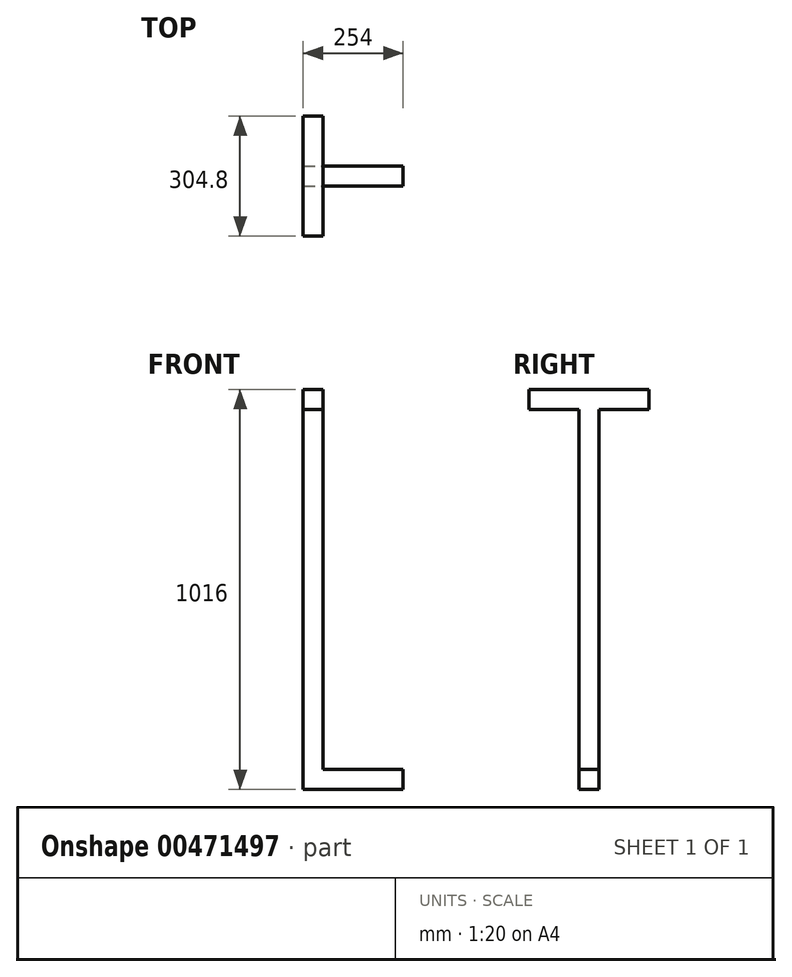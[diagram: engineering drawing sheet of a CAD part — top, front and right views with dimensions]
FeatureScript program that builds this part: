
annotation { "Feature Type Name" : "Feature", "Feature Type Description" : "" }
export const myFeature = defineFeature(function(context is Context, id is Id, definition is map)
    precondition{}
    {
        {
            var Q0;
            Q0=qCreatedBy(makeId("Front.planeOp"),FACE);
            var sketch = newSketch(context, id + "F0", { "sketchPlane" : qUnion([Q0])});
            skLineSegment(sketch, "E0", {"start": v(0, 0) * mm, "end": v(-203.2, 0) * mm});
            skLineSegment(sketch, "E1", {"start": v(-203.2, 0) * mm, "end": v(-203.2, 965.2) * mm});
            skLineSegment(sketch, "E2", {"start": v(-254, 965.2) * mm, "end": v(-254, -50.8) * mm});
            skLineSegment(sketch, "E3", {"start": v(-254, -50.8) * mm, "end": v(0, -50.8) * mm});
            skLineSegment(sketch, "E4", {"start": v(0, -50.8) * mm, "end": v(0, 0) * mm});
            skLineSegment(sketch, "E5", {"start": v(-203.2, 965.2) * mm, "end": v(-254, 965.2) * mm});
            skSolve(sketch);
        }
        {
            var Q0;
            Q0=makeQuery(id+"F0.imprint","IMPRINT",FACE,{"disambiguationData":[TD([[makeQuery(id+"F0.imprint","IMPRINT",EDGE,{"derivedFrom":sQuery(id+"F0.wireOp",EDGE,"E0")}),1.0]])]});
            extrude(context, id + "F1", {"entities" : qUnion([Q0]), "endBound" : BoundingType.SYMMETRIC, "depth" : 50.8 * mm, "offsetDistance" : 25.4 * mm});
        }
        {
            var Q0;
            Q0=makeQuery(id+"F1.opExtrude","CAP_FACE",FACE,{"disambiguationData":[OSD([sQuery(id+"F0.wireOp",EDGE,"E0"),sQuery(id+"F0.wireOp",EDGE,"E1"),sQuery(id+"F0.wireOp",EDGE,"E2"),sQuery(id+"F0.wireOp",EDGE,"E3"),sQuery(id+"F0.wireOp",EDGE,"E4"),sQuery(id+"F0.wireOp",EDGE,"E5")])],"isStart":false});
            var sketch = newSketch(context, id + "F2", { "sketchPlane" : qUnion([Q0])});
            skLineSegment(sketch, "E6.bottom", {"start": v(-254, 965.2) * mm, "end": v(-203.2, 965.2) * mm});
            skLineSegment(sketch, "E6.top", {"start": v(-254, 914.4) * mm, "end": v(-203.2, 914.4) * mm});
            skLineSegment(sketch, "E6.left", {"start": v(-254, 965.2) * mm, "end": v(-254, 914.4) * mm});
            skLineSegment(sketch, "E6.right", {"start": v(-203.2, 965.2) * mm, "end": v(-203.2, 914.4) * mm});
            skSolve(sketch);
        }
        {
            var Q0;
            Q0=makeQuery(id+"F2.imprint","IMPRINT",FACE,{"disambiguationData":[TD([[makeQuery(id+"F2.imprint","IMPRINT",EDGE,{"derivedFrom":sQuery(id+"F2.wireOp",EDGE,"E6.bottom")}),1.0]])]});
            extrude(context, id + "F3", {"entities" : qUnion([Q0]), "operationType" : NewBodyOperationType.ADD, "depth" : 127 * mm, "offsetDistance" : 25.4 * mm});
        }
        {
            var Q0;
            Q0=makeQuery(id+"F1.opExtrude","SWEPT_BODY",BODY,{"disambiguationData":[OSD([sQuery(id+"F0.wireOp",EDGE,"E0"),sQuery(id+"F0.wireOp",EDGE,"E1"),sQuery(id+"F0.wireOp",EDGE,"E2"),sQuery(id+"F0.wireOp",EDGE,"E3"),sQuery(id+"F0.wireOp",EDGE,"E4"),sQuery(id+"F0.wireOp",EDGE,"E5")])]});
            var Q1;
            Q1=qCreatedBy(makeId("Front.planeOp"),FACE);
            mirror(context, id + "F4", {"operationType" : NewBodyOperationType.ADD, "entities" : qUnion([Q0]), "mirrorPlane" : qUnion([Q1])});
        }
        {
            var Q0;
            {var subQ0=makeQuery(id+"F3.boolean.opBoolean","MERGE",FACE,{"derivedFrom":[makeQuery(id+"F1.opExtrude","SWEPT_FACE",FACE,{"disambiguationData":[OSD([sQuery(id+"F0.wireOp",EDGE,"E2")])]}),makeQuery(id+"F3.opExtrude","SWEPT_FACE",FACE,{"disambiguationData":[OSD([sQuery(id+"F2.wireOp",EDGE,"E6.left")])]})]});Q0=makeQuery(id+"F4.boolean.opBoolean","MERGE",FACE,{"derivedFrom":[subQ0,makeQuery(id+"F4.opPattern","COPY",FACE,{"derivedFrom":subQ0,"instanceName":"1"})]});}
            var sketch = newSketch(context, id + "F5", { "sketchPlane" : qUnion([Q0])});
            skCircle(sketch, "E7", {"center": v(-127, 939.8) * mm, "radius": 9.53 * mm});
            skSolve(sketch);
        }
        {
            var Q0;
            Q0=sQuery(id+"F5.wireOp",EDGE,"E7");
            extrude(context, id + "F6", {"bodyType" : ToolBodyType.SURFACE, "surfaceEntities" : qUnion([Q0]), "depth" : 406.4 * mm, "offsetDistance" : 25.4 * mm});
        }
        {
            var Q0;
            Q0=makeQuery(id+"F6.opExtrude","SWEPT_BODY",BODY,{"disambiguationData":[OSD([sQuery(id+"F5.wireOp",EDGE,"E7")])]});
            var Q1;
            Q1=qCreatedBy(makeId("Front.planeOp"),FACE);
            mirror(context, id + "F7", {"entities" : qUnion([Q0]), "mirrorPlane" : qUnion([Q1])});
        }
    });
